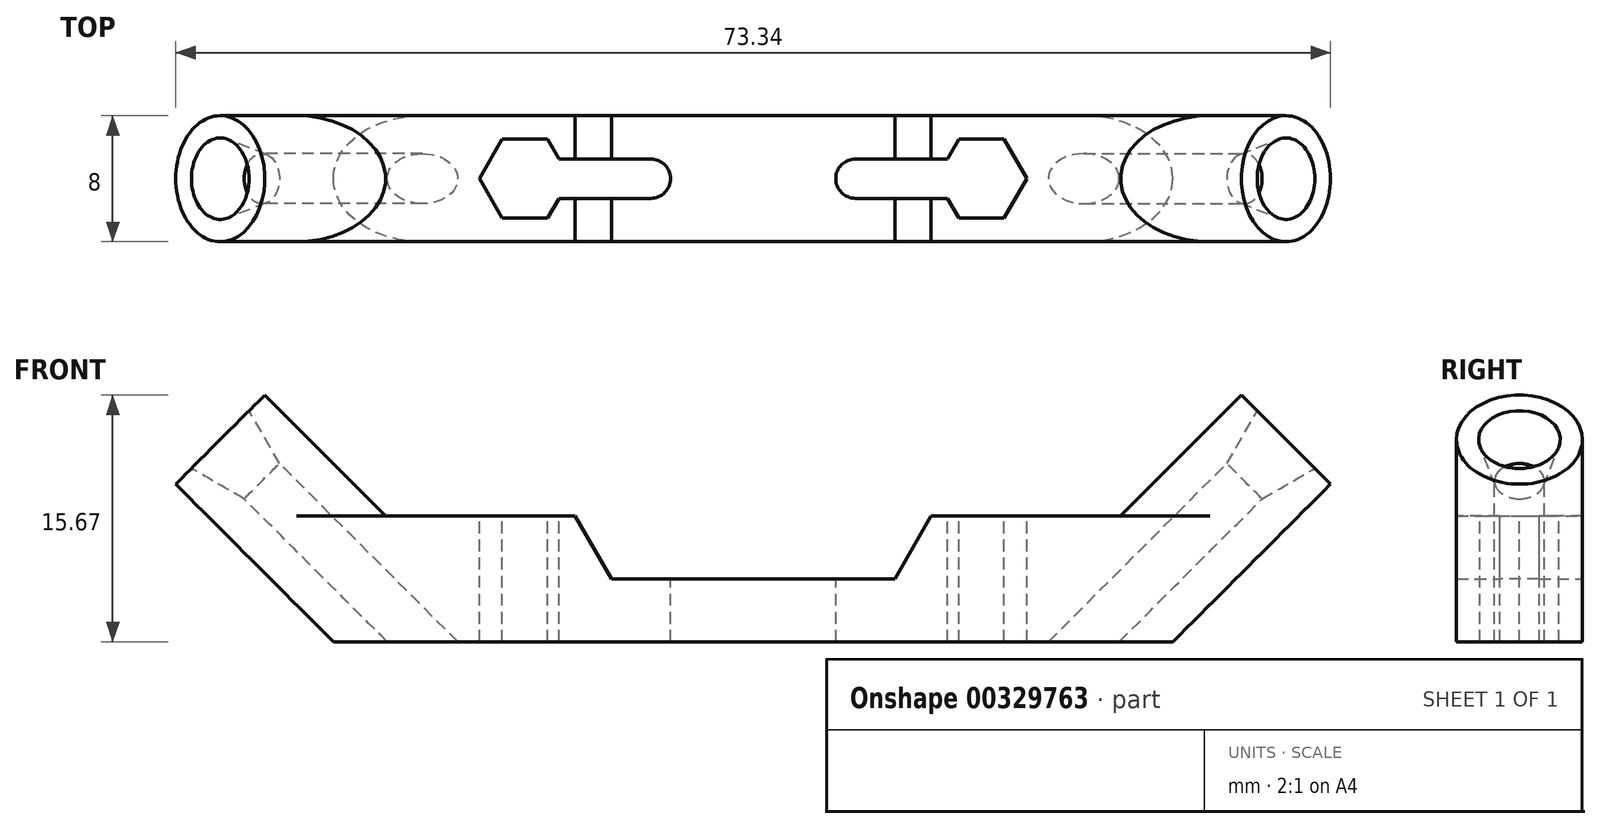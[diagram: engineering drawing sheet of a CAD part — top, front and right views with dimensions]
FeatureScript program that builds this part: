
annotation { "Feature Type Name" : "Feature", "Feature Type Description" : "" }
export const myFeature = defineFeature(function(context is Context, id is Id, definition is map)
    precondition{}
    {
        {
            var Q0;
            Q0=qCreatedBy(makeId("Front.planeOp"),FACE);
            var sketch = newSketch(context, id + "F0", { "sketchPlane" : qUnion([Q0])});
            skLineSegment(sketch, "E0", {"start": v(0, 0) * mm, "end": v(-26.66, 0) * mm});
            skLineSegment(sketch, "E1", {"start": v(-26.66, 0) * mm, "end": v(-34.66, 8) * mm});
            skLineSegment(sketch, "E2", {"start": v(-34.66, 8) * mm, "end": v(0, 8) * mm});
            skLineSegment(sketch, "E3", {"start": v(0, 8) * mm, "end": v(0, 0) * mm});
            skLineSegment(sketch, "E4", {"start": v(-29, 8) * mm, "end": v(-21, 0) * mm, "construction": true});
            skLineSegment(sketch, "E5", {"start": v(0, 8) * mm, "end": v(0, 31.76) * mm, "construction": true});
            skSolve(sketch);
        }
        {
            var Q0;
            Q0=qSketchRegion(id+"F0",true);
            extrude(context, id + "F1", {"entities" : qUnion([Q0]), "endBound" : BoundingType.SYMMETRIC, "depth" : 8 * mm});
        }
        {
            var Q0;
            Q0=makeQuery(id+"F1.opExtrude","CAP_EDGE",EDGE,{"disambiguationData":[OSD([sQuery(id+"F0.wireOp",EDGE,"E1")])],"isStart":true});
            var Q1;
            Q1=makeQuery(id+"F1.opExtrude","CAP_EDGE",EDGE,{"disambiguationData":[OSD([sQuery(id+"F0.wireOp",EDGE,"E1")])],"isStart":false});
            fillet(context, id + "F2", {"entities" : qUnion([Q0, Q1]), "radius" : 4 * mm, "tangentPropagation" : true, "allowEdgeOverflow" : false});
        }
        {
            var Q0;
            Q0=makeQuery(id+"F1.opExtrude","SWEPT_FACE",FACE,{"disambiguationData":[OSD([sQuery(id+"F0.wireOp",EDGE,"E2")])]});
            var sketch = newSketch(context, id + "F3", { "sketchPlane" : qUnion([Q0])});
            skLineSegment(sketch, "E6", {"start": v(-14.5, 0) * mm, "end": v(0, 0) * mm, "construction": true});
            skLineSegment(sketch, "E7", {"start": v(0, 0) * mm, "end": v(0, 20.84) * mm, "construction": true});
            skCircle(sketch, "E8.cCircle", {"center": v(-14.5, 0) * mm, "radius": 2.5 * mm, "construction": true});
            skLineSegment(sketch, "E8.0", {"start": v(-13.06, 2.5) * mm, "end": v(-11.61, 0) * mm});
            skLineSegment(sketch, "E8.1", {"start": v(-11.61, 0) * mm, "end": v(-13.06, -2.5) * mm});
            skLineSegment(sketch, "E8.2", {"start": v(-13.06, -2.5) * mm, "end": v(-15.94, -2.5) * mm});
            skLineSegment(sketch, "E8.3", {"start": v(-15.94, -2.5) * mm, "end": v(-17.39, 0) * mm});
            skLineSegment(sketch, "E8.4", {"start": v(-17.39, 0) * mm, "end": v(-15.94, 2.5) * mm});
            skLineSegment(sketch, "E8.5", {"start": v(-15.94, 2.5) * mm, "end": v(-13.06, 2.5) * mm});
            skPoint(sketch, "E8.0.midPoint", {"position": v(-12.33, 1.25) * mm});
            skSolve(sketch);
        }
        {
            var Q0;
            Q0=qSketchRegion(id+"F3",true);
            extrude(context, id + "F4", {"entities" : qUnion([Q0]), "operationType" : NewBodyOperationType.REMOVE, "endBound" : BoundingType.UP_TO_NEXT, "oppositeDirection" : true, "depth" : 25.4 * mm});
        }
        {
            var Q0;
            Q0=qCreatedBy(makeId("Front.planeOp"),FACE);
            var sketch = newSketch(context, id + "F5", { "sketchPlane" : qUnion([Q0])});
            skLineSegment(sketch, "E9", {"start": v(0, 11.67) * mm, "end": v(0, 4) * mm});
            skLineSegment(sketch, "E10", {"start": v(0, 4) * mm, "end": v(-9, 4) * mm});
            skLineSegment(sketch, "E11", {"start": v(-9, 4) * mm, "end": v(-13.43, 11.67) * mm});
            skLineSegment(sketch, "E12", {"start": v(-13.43, 11.67) * mm, "end": v(0, 11.67) * mm});
            skLineSegment(sketch, "E13", {"start": v(0, 11.67) * mm, "end": v(0, 17.09) * mm, "construction": true});
            skSolve(sketch);
        }
        {
            var Q0;
            Q0 = qSketchRegion(id + "F5", true);
            extrude(context, id + "F6", {"entities" : qUnion([Q0]), "operationType" : NewBodyOperationType.REMOVE, "endBound" : BoundingType.SYMMETRIC, "depth" : 25 * mm});
        }
        {
            var Q0;
            Q0=qCreatedBy(makeId("Front.planeOp"),FACE);
            var sketch = newSketch(context, id + "F7", { "sketchPlane" : qUnion([Q0])});
            skLineSegment(sketch, "E14", {"start": v(-10.3, -10.7) * mm, "end": v(-44.62, 23.62) * mm});
            skLineSegment(sketch, "E15", {"start": v(-44.62, 23.62) * mm, "end": v(-45.74, 22.5) * mm});
            skLineSegment(sketch, "E16", {"start": v(-45.74, 22.5) * mm, "end": v(-11.43, -11.81) * mm});
            skLineSegment(sketch, "E17", {"start": v(-11.43, -11.81) * mm, "end": v(-10.3, -10.7) * mm});
            skLineSegment(sketch, "E18", {"start": v(-38.6, 17.6) * mm, "end": v(-44.62, 23.62) * mm, "construction": true});
            skSolve(sketch);
        }
        {
            var Q0;
            Q0=sQuery(id+"F0.wireOp",EDGE,"E4");
            var Q1;
            Q1=sQuery(id+"F0.wireOp",VERTEX,"E4.start");
            cPlane(context, id + "F8", {"entities" : qUnion([Q0, Q1]), "cplaneType" : CPlaneType.LINE_POINT, "offset" : 25 * mm, "width" : 150 * mm, "height" : 150 * mm});
        }
        {
            var Q0;
            Q0=qCreatedBy(id+"F8.planeOp",FACE);
            var sketch = newSketch(context, id + "F9", { "sketchPlane" : qUnion([Q0])});
            skCircle(sketch, "E19", {"center": v(0, -14.85) * mm, "radius": 4 * mm});
            skSolve(sketch);
        }
        {
            var Q0;
            Q0=qSketchRegion(id+"F9",true);
            extrude(context, id + "F10", {"entities" : qUnion([Q0]), "operationType" : NewBodyOperationType.ADD, "endBound" : BoundingType.SYMMETRIC, "oppositeDirection" : true, "depth" : 13.7 * mm});
        }
        {
            var Q0;
            Q0=qSketchRegion(id+"F7",true);
            var Q1;
            Q1=sQuery(id+"F7.wireOp",EDGE,"E14");
            revolve(context, id + "F11", {"operationType" : NewBodyOperationType.REMOVE, "entities" : qUnion([Q0]), "axis" : qUnion([Q1]), "revolveType" : RevolveType.FULL, "oppositeDirection" : true});
        }
        {
            var Q0;
            Q0=makeQuery(id+"F11.boolean.opBoolean","INTERSECT",EDGE,{"derivedFrom":[makeQuery(id+"F10.opExtrude","CAP_FACE",FACE,{"disambiguationData":[OSD([sQuery(id+"F9.wireOp",EDGE,"E19")])],"isStart":false}),makeQuery(id+"F11.opRevolve","SWEPT_FACE",FACE,{"disambiguationData":[OSD([sQuery(id+"F7.wireOp",EDGE,"E16")])]})]});
            chamfer(context, id + "F12", {"entities" : qUnion([Q0]), "chamferType" : ChamferType.OFFSET_ANGLE, "width" : 1 * mm, "oppositeDirection" : false, "angle" : 75 * degree, "tangentPropagation" : true});
        }
        {
            var Q0;
            Q0=makeQuery(id+"F1.opExtrude","SWEPT_FACE",FACE,{"disambiguationData":[OSD([sQuery(id+"F0.wireOp",EDGE,"E2")])]});
            var sketch = newSketch(context, id + "F13", { "sketchPlane" : qUnion([Q0])});
            skLineSegment(sketch, "E20", {"start": v(-14.5, 0) * mm, "end": v(-6.5, 0) * mm});
            skArc(sketch, "E21.0.startCap", {"start": v(-14.5, -1.25) * mm, "mid": v(-15.75, 0) * mm, "end": v(-14.5, 1.25) * mm});
            skArc(sketch, "E21.0.endCap", {"start": v(-6.5, 1.25) * mm, "mid": v(-5.25, 0) * mm, "end": v(-6.5, -1.25) * mm});
            skLineSegment(sketch, "E21.0.left", {"start": v(-14.5, 1.25) * mm, "end": v(-6.5, 1.25) * mm});
            skLineSegment(sketch, "E21.0.right", {"start": v(-14.5, -1.25) * mm, "end": v(-6.5, -1.25) * mm});
            skPoint(sketch, "E22", {"position": v(-14.5, 2.5) * mm});
            skSolve(sketch);
        }
        {
            var Q0;
            Q0 = qSketchRegion(id + "F13", true);
            extrude(context, id + "F14", {"entities" : qUnion([Q0]), "operationType" : NewBodyOperationType.REMOVE, "endBound" : BoundingType.THROUGH_ALL, "oppositeDirection" : true, "depth" : 25 * mm});
        }
        {
            var Q0;
            Q0=makeQuery(id+"F1.opExtrude","SWEPT_BODY",BODY,{"disambiguationData":[OSD([sQuery(id+"F0.wireOp",EDGE,"E0"),sQuery(id+"F0.wireOp",EDGE,"E1"),sQuery(id+"F0.wireOp",EDGE,"E2"),sQuery(id+"F0.wireOp",EDGE,"E3")])]});
            var Q1;
            Q1=makeQuery(id+"F1.opExtrude","SWEPT_FACE",FACE,{"disambiguationData":[OSD([sQuery(id+"F0.wireOp",EDGE,"E3")])]});
            mirror(context, id + "F15", {"operationType" : NewBodyOperationType.ADD, "entities" : qUnion([Q0]), "mirrorPlane" : qUnion([Q1])});
        }
    });
